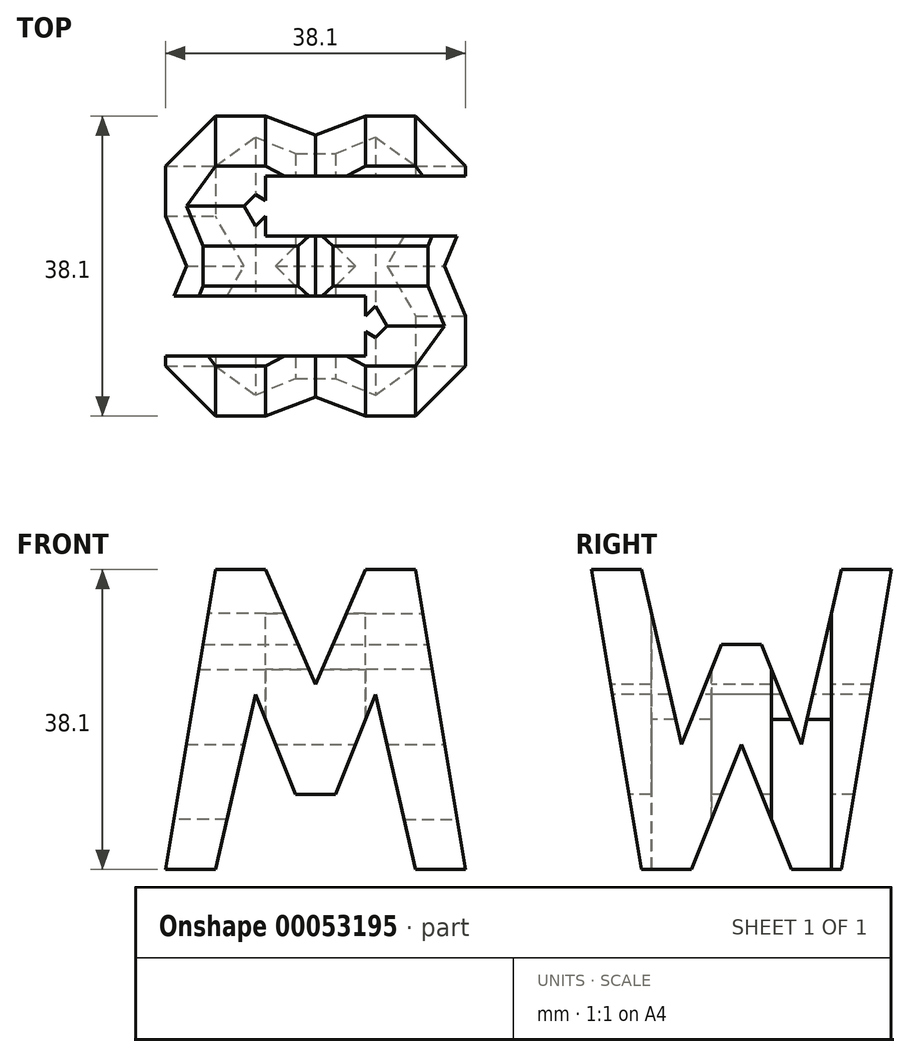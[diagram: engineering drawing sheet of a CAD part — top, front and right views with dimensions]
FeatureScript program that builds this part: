
annotation { "Feature Type Name" : "Feature", "Feature Type Description" : "" }
export const myFeature = defineFeature(function(context is Context, id is Id, definition is map)
    precondition{}
    {
        {
            var Q0;
            Q0=qCreatedBy(makeId("Front.planeOp"),FACE);
            cPlane(context, id + "F0", {"entities" : qUnion([Q0]), "cplaneType" : CPlaneType.OFFSET, "offset" : 0 * mm, "width" : 152.4 * mm, "height" : 152.4 * mm});
        }
        {
            var Q0;
            Q0=qCreatedBy(makeId("Right.planeOp"),FACE);
            cPlane(context, id + "F1", {"entities" : qUnion([Q0]), "cplaneType" : CPlaneType.OFFSET, "offset" : 38.1 * mm, "width" : 152.4 * mm, "height" : 152.4 * mm});
        }
        {
            var Q0;
            Q0=qCreatedBy(makeId("Top.planeOp"),FACE);
            cPlane(context, id + "F2", {"entities" : qUnion([Q0]), "cplaneType" : CPlaneType.OFFSET, "offset" : 38.1 * mm, "width" : 152.4 * mm, "height" : 152.4 * mm});
        }
        {
            var Q0;
            Q0=qCreatedBy(makeId("Front.planeOp"),FACE);
            var sketch = newSketch(context, id + "F3", { "sketchPlane" : qUnion([Q0])});
            skLineSegment(sketch, "E0.bottom", {"start": v(0, 0) * mm, "end": v(38.1, 0) * mm});
            skLineSegment(sketch, "E0.top", {"start": v(0, 38.1) * mm, "end": v(38.1, 38.1) * mm});
            skLineSegment(sketch, "E0.left", {"start": v(0, 0) * mm, "end": v(0, 38.1) * mm});
            skLineSegment(sketch, "E0.right", {"start": v(38.1, 0) * mm, "end": v(38.1, 38.1) * mm});
            skSolve(sketch);
        }
        {
            var Q0;
            Q0 = qSketchRegion(id + "F3", true);
            extrude(context, id + "F4", {"entities" : qUnion([Q0]), "oppositeDirection" : true, "depth" : 38.1 * mm});
        }
        {
            var Q0;
            Q0=qCreatedBy(id+"F1.planeOp",FACE);
            var sketch = newSketch(context, id + "F5", { "sketchPlane" : qUnion([Q0])});
            skLineSegment(sketch, "E1.bottom", {"start": v(0, 0) * mm, "end": v(38.1, 0) * mm});
            skLineSegment(sketch, "E1.top", {"start": v(0, 38.1) * mm, "end": v(38.1, 38.1) * mm});
            skLineSegment(sketch, "E1.left", {"start": v(0, 0) * mm, "end": v(0, 38.1) * mm});
            skLineSegment(sketch, "E1.right", {"start": v(38.1, 0) * mm, "end": v(38.1, 38.1) * mm});
            skLineSegment(sketch, "E2", {"start": v(0, 38.1) * mm, "end": v(6.35, 0) * mm});
            skLineSegment(sketch, "E3", {"start": v(6.35, 38.1) * mm, "end": v(11.43, 15.88) * mm});
            skLineSegment(sketch, "E4", {"start": v(11.43, 15.88) * mm, "end": v(16.5, 28.58) * mm});
            skLineSegment(sketch, "E5", {"start": v(16.5, 28.58) * mm, "end": v(21.59, 28.58) * mm});
            skLineSegment(sketch, "E6", {"start": v(21.6, 28.58) * mm, "end": v(26.67, 15.88) * mm});
            skLineSegment(sketch, "E7", {"start": v(26.67, 15.88) * mm, "end": v(31.75, 38.1) * mm});
            skLineSegment(sketch, "E8", {"start": v(31.75, 38.1) * mm, "end": v(38.1, 38.1) * mm});
            skLineSegment(sketch, "E9", {"start": v(38.1, 38.1) * mm, "end": v(31.75, 0) * mm});
            skLineSegment(sketch, "E10", {"start": v(31.75, 0) * mm, "end": v(25.4, 0) * mm});
            skLineSegment(sketch, "E11", {"start": v(25.4, 0) * mm, "end": v(19.05, 15.88) * mm});
            skLineSegment(sketch, "E12", {"start": v(19.05, 15.88) * mm, "end": v(12.7, 0) * mm});
            skSolve(sketch);
        }
        {
            var Q0;
            {var subQ0=sQuery(id+"F5.wireOp",EDGE,"E3");Q0=makeQuery(id+"F5.imprint","IMPRINT",FACE,{"disambiguationData":[TD([[makeQuery(id+"F5.imprint","IMPRINT",EDGE,{"derivedFrom":subQ0}),1.0]])]});}
            var Q1;
            {var subQ0=sQuery(id+"F5.wireOp",EDGE,"E1.left");Q1=makeQuery(id+"F5.imprint","IMPRINT",FACE,{"disambiguationData":[TD([[makeQuery(id+"F5.imprint","IMPRINT",EDGE,{"derivedFrom":subQ0}),-1.0]])]});}
            var Q2;
            {var subQ0=sQuery(id+"F5.wireOp",EDGE,"E11");Q2=makeQuery(id+"F5.imprint","IMPRINT",FACE,{"disambiguationData":[TD([[makeQuery(id+"F5.imprint","IMPRINT",EDGE,{"derivedFrom":subQ0}),1.0]])]});}
            var Q3;
            {var subQ0=sQuery(id+"F5.wireOp",EDGE,"E1.right");Q3=makeQuery(id+"F5.imprint","IMPRINT",FACE,{"disambiguationData":[TD([[makeQuery(id+"F5.imprint","IMPRINT",EDGE,{"derivedFrom":subQ0}),1.0]])]});}
            extrude(context, id + "F6", {"entities" : qUnion([Q0, Q1, Q2, Q3]), "operationType" : NewBodyOperationType.REMOVE, "oppositeDirection" : true, "depth" : 38.1 * mm});
        }
        {
            var Q0;
            Q0=qCreatedBy(id+"F0.planeOp",FACE);
            var sketch = newSketch(context, id + "F7", { "sketchPlane" : qUnion([Q0])});
            skLineSegment(sketch, "E13", {"start": v(0, 38.1) * mm, "end": v(0, 0) * mm});
            skLineSegment(sketch, "E14", {"start": v(0, 0) * mm, "end": v(38.1, 0) * mm});
            skLineSegment(sketch, "E15", {"start": v(38.1, 0) * mm, "end": v(38.1, 38.1) * mm});
            skLineSegment(sketch, "E16", {"start": v(38.1, 38.1) * mm, "end": v(0, 38.1) * mm});
            skLineSegment(sketch, "E17", {"start": v(6.35, 38.1) * mm, "end": v(0, 0) * mm});
            skLineSegment(sketch, "E18", {"start": v(6.35, 0) * mm, "end": v(11.43, 22.23) * mm});
            skLineSegment(sketch, "E19", {"start": v(11.43, 22.23) * mm, "end": v(16.51, 9.53) * mm});
            skLineSegment(sketch, "E20", {"start": v(16.51, 9.53) * mm, "end": v(21.59, 9.53) * mm});
            skLineSegment(sketch, "E21", {"start": v(21.59, 9.53) * mm, "end": v(26.67, 22.22) * mm});
            skLineSegment(sketch, "E22", {"start": v(26.67, 22.22) * mm, "end": v(31.75, 0) * mm});
            skLineSegment(sketch, "E23", {"start": v(31.75, 0) * mm, "end": v(38.1, 0) * mm});
            skLineSegment(sketch, "E24", {"start": v(31.75, 38.1) * mm, "end": v(38.1, 0) * mm});
            skLineSegment(sketch, "E25", {"start": v(25.4, 38.1) * mm, "end": v(19.05, 23.51) * mm});
            skLineSegment(sketch, "E26", {"start": v(19.05, 23.51) * mm, "end": v(12.7, 38.1) * mm});
            skSolve(sketch);
        }
        {
            var Q0;
            {var subQ0=sQuery(id+"F7.wireOp",EDGE,"E25");Q0=makeQuery(id+"F7.imprint","IMPRINT",FACE,{"disambiguationData":[TD([[makeQuery(id+"F7.imprint","IMPRINT",EDGE,{"derivedFrom":subQ0}),-1.0]])]});}
            var Q1;
            {var subQ0=sQuery(id+"F7.wireOp",EDGE,"E13");Q1=makeQuery(id+"F7.imprint","IMPRINT",FACE,{"disambiguationData":[TD([[makeQuery(id+"F7.imprint","IMPRINT",EDGE,{"derivedFrom":subQ0}),1.0]])]});}
            var Q2;
            {var subQ0=sQuery(id+"F7.wireOp",EDGE,"E18");Q2=makeQuery(id+"F7.imprint","IMPRINT",FACE,{"disambiguationData":[TD([[makeQuery(id+"F7.imprint","IMPRINT",EDGE,{"derivedFrom":subQ0}),-1.0]])]});}
            var Q3;
            {var subQ0=sQuery(id+"F7.wireOp",EDGE,"E15");Q3=makeQuery(id+"F7.imprint","IMPRINT",FACE,{"disambiguationData":[TD([[makeQuery(id+"F7.imprint","IMPRINT",EDGE,{"derivedFrom":subQ0}),1.0]])]});}
            extrude(context, id + "F8", {"entities" : qUnion([Q0, Q1, Q2, Q3]), "operationType" : NewBodyOperationType.REMOVE, "oppositeDirection" : true, "depth" : 38.1 * mm});
        }
        {
            var Q0;
            Q0=qCreatedBy(id+"F2.planeOp",FACE);
            var sketch = newSketch(context, id + "F9", { "sketchPlane" : qUnion([Q0])});
            skLineSegment(sketch, "E27", {"start": v(0, 0) * mm, "end": v(0, 38.1) * mm});
            skLineSegment(sketch, "E28", {"start": v(0, 38.1) * mm, "end": v(38.1, 38.1) * mm});
            skLineSegment(sketch, "E29", {"start": v(38.1, 38.1) * mm, "end": v(38.1, 0) * mm});
            skLineSegment(sketch, "E30", {"start": v(38.1, 0) * mm, "end": v(0, 0) * mm});
            skLineSegment(sketch, "E31", {"start": v(38.1, 30.48) * mm, "end": v(12.7, 30.48) * mm});
            skLineSegment(sketch, "E32", {"start": v(12.7, 30.48) * mm, "end": v(12.7, 22.86) * mm});
            skLineSegment(sketch, "E33", {"start": v(12.7, 22.86) * mm, "end": v(38.1, 22.86) * mm});
            skLineSegment(sketch, "E34", {"start": v(0, 7.62) * mm, "end": v(25.4, 7.62) * mm});
            skLineSegment(sketch, "E35", {"start": v(25.4, 7.62) * mm, "end": v(25.4, 15.24) * mm});
            skLineSegment(sketch, "E36", {"start": v(25.4, 15.24) * mm, "end": v(0, 15.24) * mm});
            skSolve(sketch);
        }
        {
            var Q0;
            {var subQ0=sQuery(id+"F9.wireOp",EDGE,"E31");Q0=makeQuery(id+"F9.imprint","IMPRINT",FACE,{"disambiguationData":[TD([[makeQuery(id+"F9.imprint","IMPRINT",EDGE,{"derivedFrom":subQ0}),1.0]])]});}
            var Q1;
            {var subQ0=sQuery(id+"F9.wireOp",EDGE,"E34");Q1=makeQuery(id+"F9.imprint","IMPRINT",FACE,{"disambiguationData":[TD([[makeQuery(id+"F9.imprint","IMPRINT",EDGE,{"derivedFrom":subQ0}),1.0]])]});}
            extrude(context, id + "F10", {"entities" : qUnion([Q0, Q1]), "operationType" : NewBodyOperationType.REMOVE, "oppositeDirection" : true, "depth" : 38.1 * mm});
        }
    });
